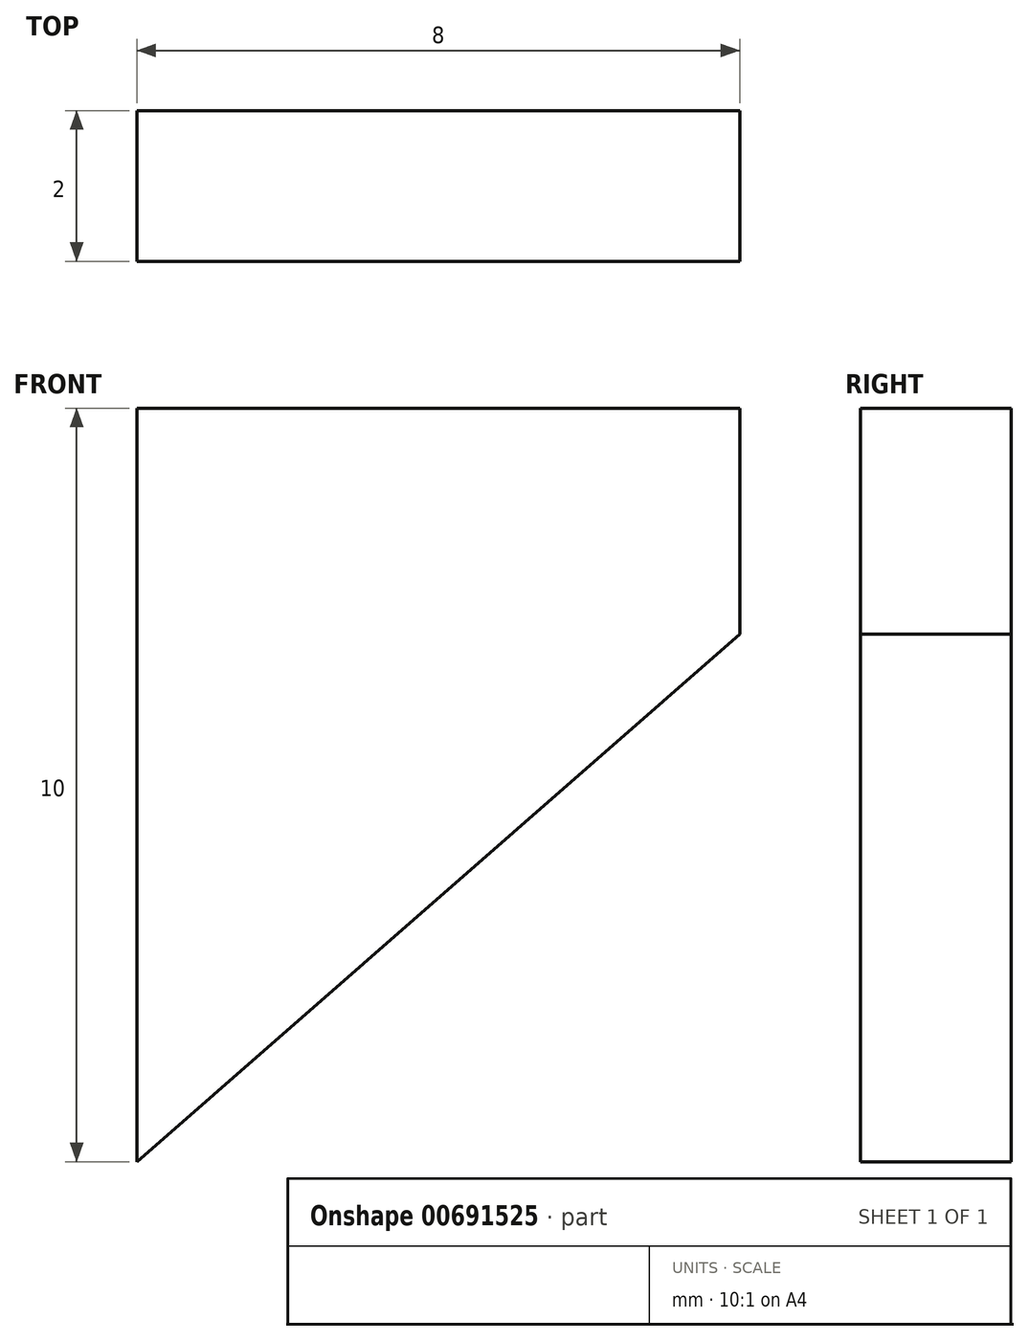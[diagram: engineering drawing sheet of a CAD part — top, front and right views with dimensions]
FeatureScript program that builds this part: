
annotation { "Feature Type Name" : "Feature", "Feature Type Description" : "" }
export const myFeature = defineFeature(function(context is Context, id is Id, definition is map)
    precondition{}
    {
        {
            var Q0;
            Q0=qCreatedBy(makeId("Front.planeOp"),FACE);
            var sketch = newSketch(context, id + "F0", { "sketchPlane" : qUnion([Q0])});
            skLineSegment(sketch, "E0", {"start": v(0, 0) * mm, "end": v(0, 10) * mm});
            skLineSegment(sketch, "E1", {"start": v(0, 10) * mm, "end": v(8, 10) * mm});
            skLineSegment(sketch, "E2", {"start": v(8, 10) * mm, "end": v(8, 7) * mm});
            skLineSegment(sketch, "E3", {"start": v(8, 7) * mm, "end": v(0, 0) * mm});
            skSolve(sketch);
        }
        {
            var Q0;
            Q0 = qSketchRegion(id + "F0", true);
            extrude(context, id + "F1", {"entities" : qUnion([Q0]), "depth" : 2 * mm, "offsetDistance" : 25 * mm});
        }
    });
